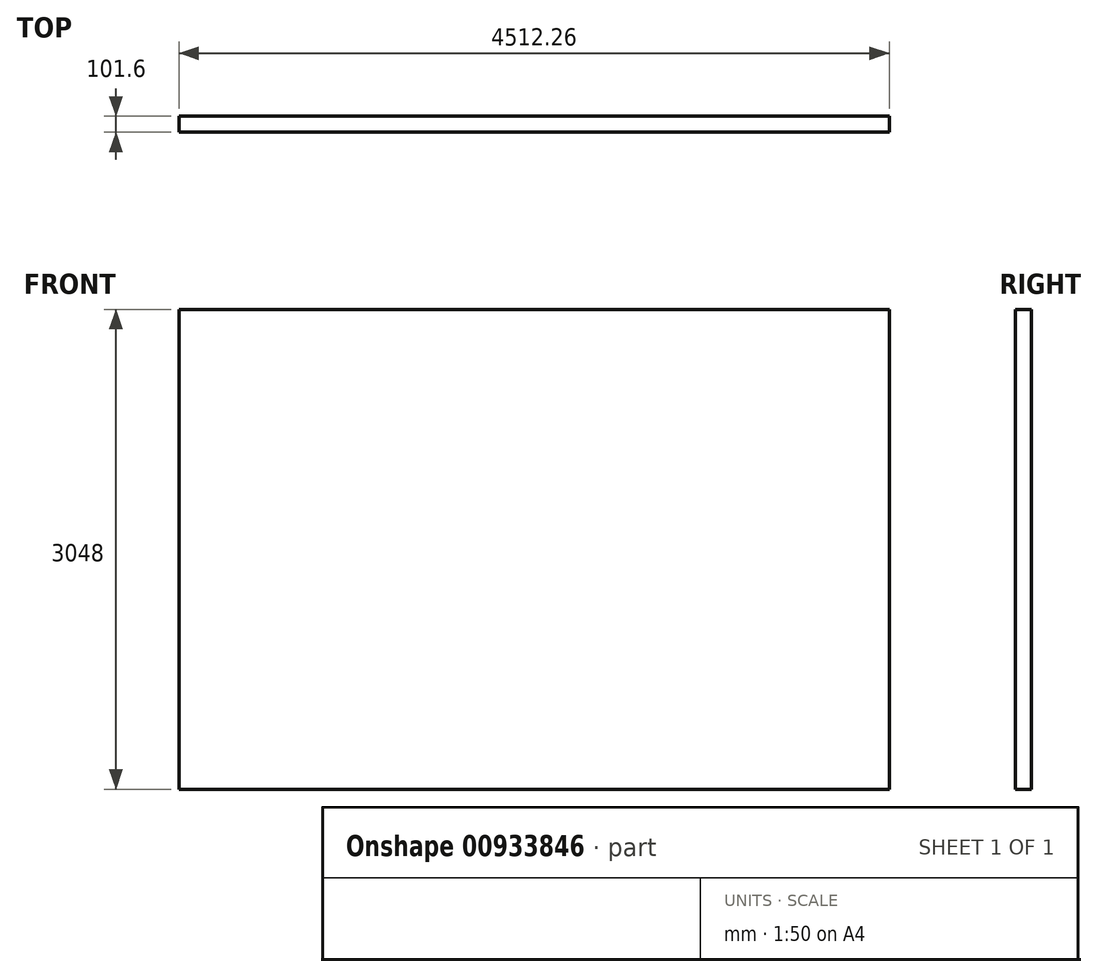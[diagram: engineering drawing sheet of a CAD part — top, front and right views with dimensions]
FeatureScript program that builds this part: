
annotation { "Feature Type Name" : "Feature", "Feature Type Description" : "" }
export const myFeature = defineFeature(function(context is Context, id is Id, definition is map)
    precondition{}
    {
        {
            var Q0;
            Q0=qCreatedBy(makeId("Front.planeOp"),FACE);
            var sketch = newSketch(context, id + "F0", { "sketchPlane" : qUnion([Q0])});
            skLineSegment(sketch, "E0.rect.bottom", {"start": v(2256.13, 1524) * mm, "end": v(-2256.13, 1524) * mm});
            skLineSegment(sketch, "E0.rect.top", {"start": v(2256.13, -1524) * mm, "end": v(-2256.13, -1524) * mm});
            skLineSegment(sketch, "E0.rect.left", {"start": v(2256.13, 1524) * mm, "end": v(2256.13, -1524) * mm});
            skLineSegment(sketch, "E0.rect.right", {"start": v(-2256.13, 1524) * mm, "end": v(-2256.13, -1524) * mm});
            skPoint(sketch, "E0.rect.middle", {"position": v(0, 0) * mm});
            skSolve(sketch);
        }
        {
            var Q0;
            Q0=qSketchRegion(id+"F0",true);
            extrude(context, id + "F1", {"entities" : qUnion([Q0]), "depth" : 101.6 * mm});
        }
    });
